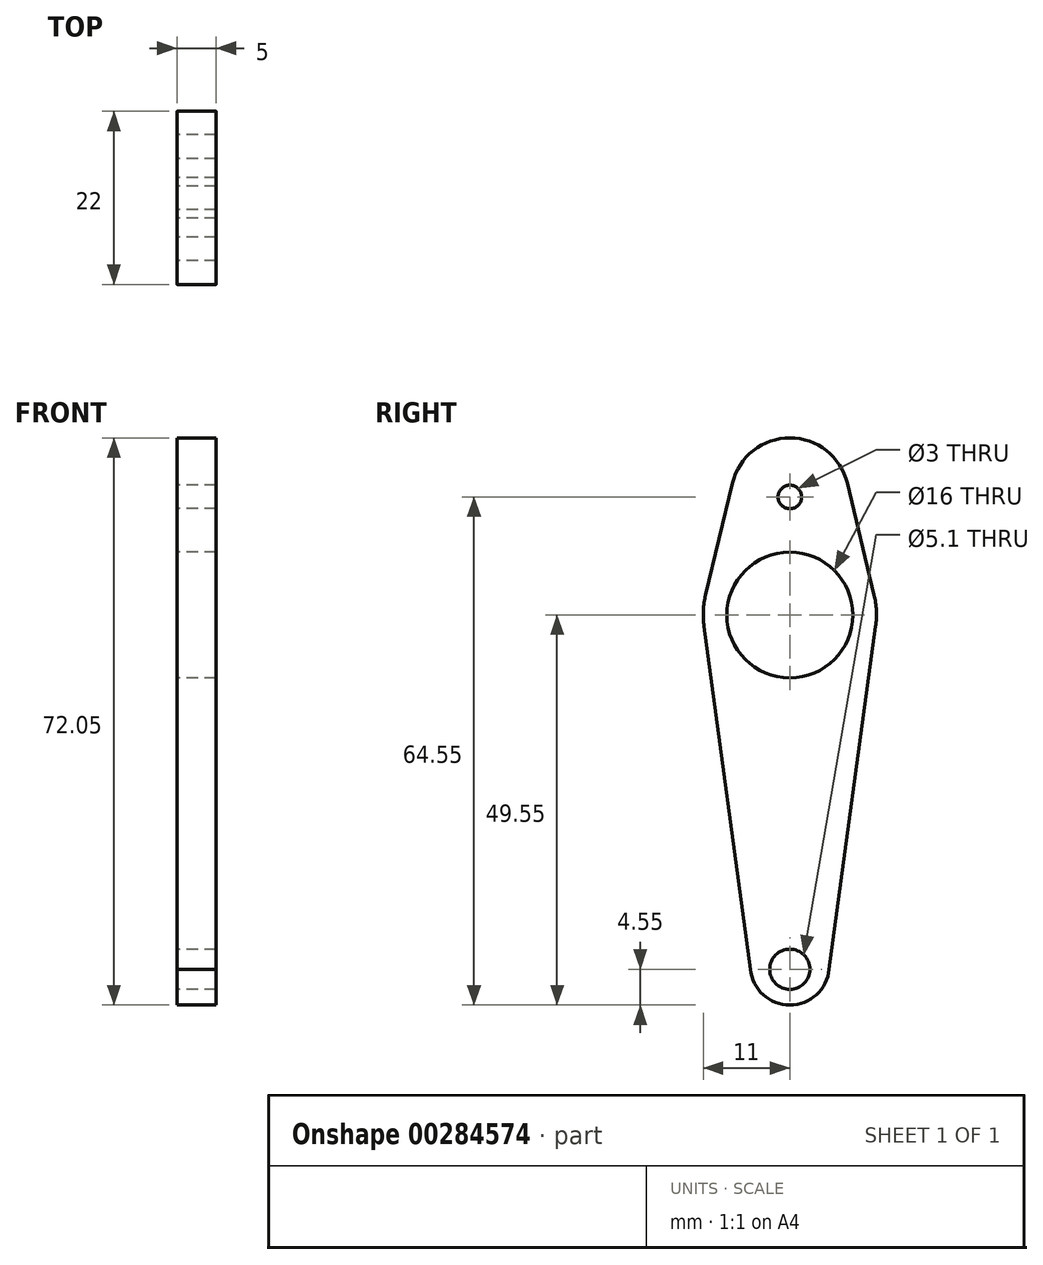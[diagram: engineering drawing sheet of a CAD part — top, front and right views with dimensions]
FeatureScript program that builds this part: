
annotation { "Feature Type Name" : "Feature", "Feature Type Description" : "" }
export const myFeature = defineFeature(function(context is Context, id is Id, definition is map)
    precondition{}
    {
        {
            var Q0;
            Q0=qCreatedBy(makeId("Right.planeOp"),FACE);
            var sketch = newSketch(context, id + "F0", { "sketchPlane" : qUnion([Q0])});
            skLineSegment(sketch, "E0", {"start": v(0, 0) * mm, "end": v(0, 15) * mm, "construction": true});
            skCircle(sketch, "E1", {"center": v(0, 15) * mm, "radius": 1.5 * mm});
            skCircle(sketch, "E2", {"center": v(0, 0) * mm, "radius": 8 * mm});
            skCircle(sketch, "E3", {"center": v(0, -45) * mm, "radius": 2.55 * mm});
            skLineSegment(sketch, "E4", {"start": v(0, 15) * mm, "end": v(7.71, 15) * mm, "construction": true});
            skLineSegment(sketch, "E5", {"start": v(0, 15) * mm, "end": v(-7.71, 15) * mm, "construction": true});
            skArc(sketch, "E6", {"start": v(7.3, 16.75) * mm, "mid": v(0, 22.5) * mm, "end": v(-7.3, 16.75) * mm});
            skArc(sketch, "E7", {"start": v(-10.7, 2.57) * mm, "mid": v(-10.99, 0.55) * mm, "end": v(-10.9, -1.48) * mm});
            skLineSegment(sketch, "E8", {"start": v(-7.3, 16.75) * mm, "end": v(-10.7, 2.57) * mm});
            skLineSegment(sketch, "E9", {"start": v(7.3, 16.75) * mm, "end": v(10.7, 2.57) * mm});
            skLineSegment(sketch, "E10", {"start": v(-5, -45) * mm, "end": v(-10.9, -1.48) * mm});
            skLineSegment(sketch, "E11", {"start": v(5, -45) * mm, "end": v(10.9, -1.48) * mm});
            skArc(sketch, "E12.trimOffspring", {"start": v(10.9, -1.48) * mm, "mid": v(10.99, 0.55) * mm, "end": v(10.7, 2.57) * mm});
            skLineSegment(sketch, "E13", {"start": v(-5, -45) * mm, "end": v(5, -45) * mm, "construction": true});
            skArc(sketch, "E14", {"start": v(-5, -45) * mm, "mid": v(0, -49.55) * mm, "end": v(5, -45) * mm});
            skSolve(sketch);
        }
        {
            var Q0;
            Q0=qSketchRegion(id+"F0",true);
            extrude(context, id + "F1", {"entities" : qUnion([Q0]), "depth" : 5 * mm});
        }
    });
